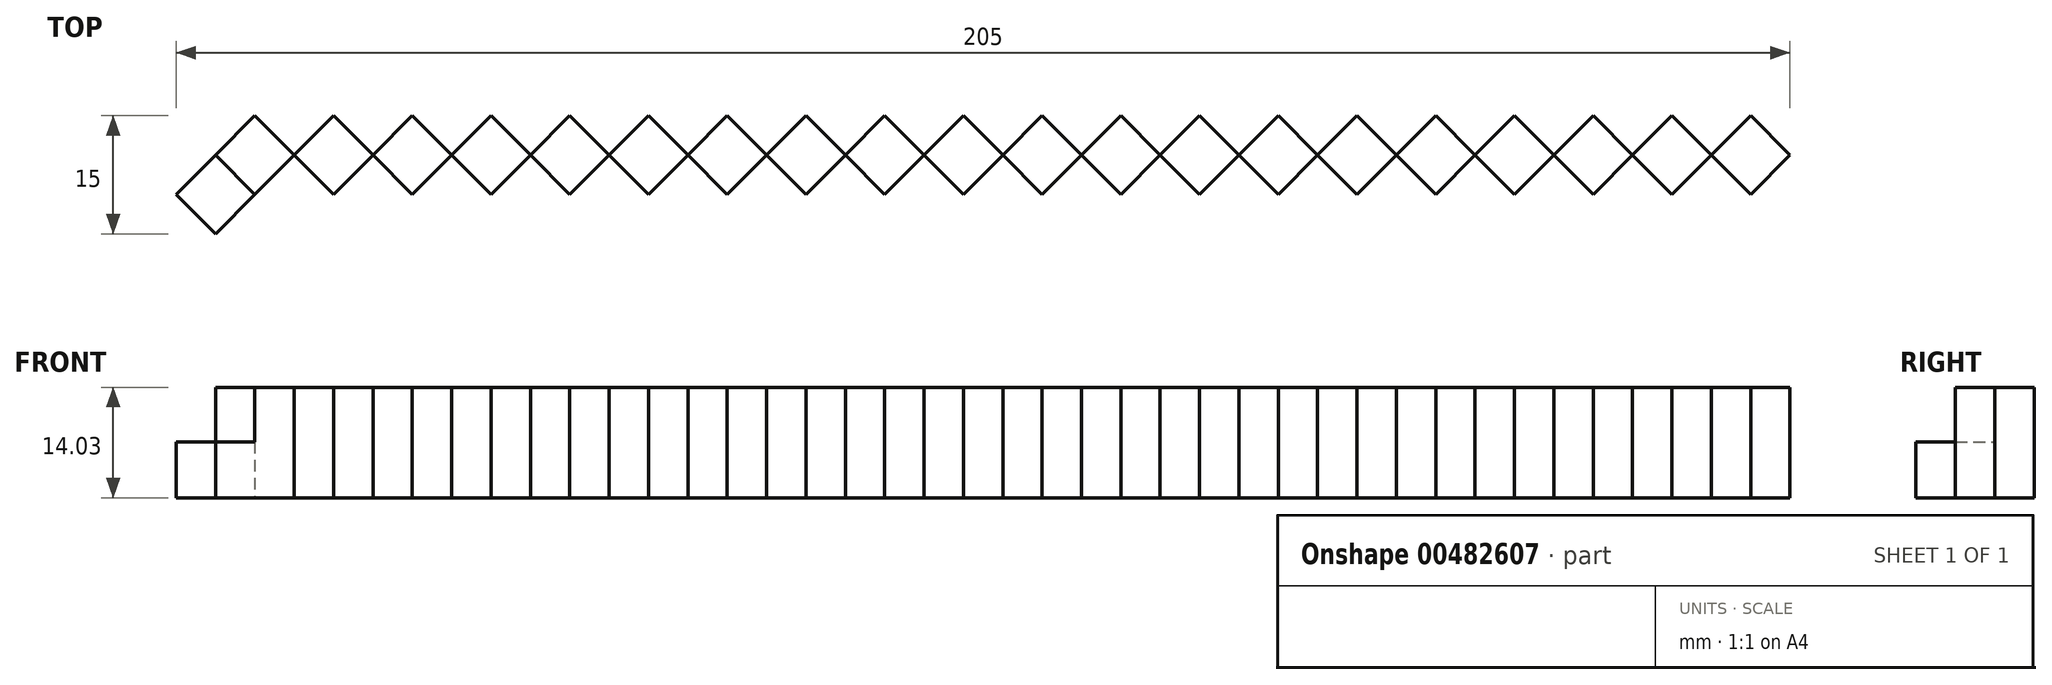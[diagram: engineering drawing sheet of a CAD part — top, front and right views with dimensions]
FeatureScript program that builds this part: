
annotation { "Feature Type Name" : "Feature", "Feature Type Description" : "" }
export const myFeature = defineFeature(function(context is Context, id is Id, definition is map)
    precondition{}
    {
        {
            var Q0;
            Q0=qCreatedBy(makeId("Top.planeOp"),FACE);
            var sketch = newSketch(context, id + "F0", { "sketchPlane" : qUnion([Q0])});
            skLineSegment(sketch, "E0", {"start": v(0, 5) * mm, "end": v(5, 0) * mm});
            skLineSegment(sketch, "E1", {"start": v(5, 0) * mm, "end": v(0, -5) * mm});
            skLineSegment(sketch, "E2", {"start": v(0, -5) * mm, "end": v(-5, 0) * mm});
            skLineSegment(sketch, "E3", {"start": v(-5, 0) * mm, "end": v(0, 5) * mm});
            skLineSegment(sketch, "E4", {"start": v(0, 5) * mm, "end": v(5, 10) * mm});
            skLineSegment(sketch, "E5", {"start": v(5, 10) * mm, "end": v(10, 5) * mm});
            skLineSegment(sketch, "E6", {"start": v(10, 5) * mm, "end": v(5, 0) * mm});
            skLineSegment(sketch, "E7.1.0.0", {"start": v(5, 0) * mm, "end": v(10, 5) * mm});
            skLineSegment(sketch, "E7.1.0.1", {"start": v(15, 0) * mm, "end": v(10, -5) * mm});
            skLineSegment(sketch, "E7.1.0.2", {"start": v(10, -5) * mm, "end": v(5, 0) * mm});
            skLineSegment(sketch, "E7.1.0.3", {"start": v(20, 5) * mm, "end": v(15, 0) * mm});
            skLineSegment(sketch, "E7.1.0.4", {"start": v(10, 5) * mm, "end": v(15, 0) * mm});
            skLineSegment(sketch, "E7.1.0.5", {"start": v(15, 10) * mm, "end": v(20, 5) * mm});
            skLineSegment(sketch, "E7.1.0.6", {"start": v(10, 5) * mm, "end": v(15, 10) * mm});
            skLineSegment(sketch, "E7.2.0.0", {"start": v(15, 0) * mm, "end": v(20, 5) * mm});
            skLineSegment(sketch, "E7.2.0.1", {"start": v(25, 0) * mm, "end": v(20, -5) * mm});
            skLineSegment(sketch, "E7.2.0.2", {"start": v(20, -5) * mm, "end": v(15, 0) * mm});
            skLineSegment(sketch, "E7.2.0.3", {"start": v(30, 5) * mm, "end": v(25, 0) * mm});
            skLineSegment(sketch, "E7.2.0.4", {"start": v(20, 5) * mm, "end": v(25, 0) * mm});
            skLineSegment(sketch, "E7.2.0.5", {"start": v(25, 10) * mm, "end": v(30, 5) * mm});
            skLineSegment(sketch, "E7.2.0.6", {"start": v(20, 5) * mm, "end": v(25, 10) * mm});
            skLineSegment(sketch, "E7.3.0.0", {"start": v(25, 0) * mm, "end": v(30, 5) * mm});
            skLineSegment(sketch, "E7.3.0.1", {"start": v(35, 0) * mm, "end": v(30, -5) * mm});
            skLineSegment(sketch, "E7.3.0.2", {"start": v(30, -5) * mm, "end": v(25, 0) * mm});
            skLineSegment(sketch, "E7.3.0.3", {"start": v(40, 5) * mm, "end": v(35, 0) * mm});
            skLineSegment(sketch, "E7.3.0.4", {"start": v(30, 5) * mm, "end": v(35, 0) * mm});
            skLineSegment(sketch, "E7.3.0.5", {"start": v(35, 10) * mm, "end": v(40, 5) * mm});
            skLineSegment(sketch, "E7.3.0.6", {"start": v(30, 5) * mm, "end": v(35, 10) * mm});
            skLineSegment(sketch, "E7.4.0.0", {"start": v(35, 0) * mm, "end": v(40, 5) * mm});
            skLineSegment(sketch, "E7.4.0.1", {"start": v(45, 0) * mm, "end": v(40, -5) * mm});
            skLineSegment(sketch, "E7.4.0.2", {"start": v(40, -5) * mm, "end": v(35, 0) * mm});
            skLineSegment(sketch, "E7.4.0.3", {"start": v(50, 5) * mm, "end": v(45, 0) * mm});
            skLineSegment(sketch, "E7.4.0.4", {"start": v(40, 5) * mm, "end": v(45, 0) * mm});
            skLineSegment(sketch, "E7.4.0.5", {"start": v(45, 10) * mm, "end": v(50, 5) * mm});
            skLineSegment(sketch, "E7.4.0.6", {"start": v(40, 5) * mm, "end": v(45, 10) * mm});
            skLineSegment(sketch, "E7.5.0.0", {"start": v(45, 0) * mm, "end": v(50, 5) * mm});
            skLineSegment(sketch, "E7.5.0.1", {"start": v(55, 0) * mm, "end": v(50, -5) * mm});
            skLineSegment(sketch, "E7.5.0.2", {"start": v(50, -5) * mm, "end": v(45, 0) * mm});
            skLineSegment(sketch, "E7.5.0.3", {"start": v(60, 5) * mm, "end": v(55, 0) * mm});
            skLineSegment(sketch, "E7.5.0.4", {"start": v(50, 5) * mm, "end": v(55, 0) * mm});
            skLineSegment(sketch, "E7.5.0.5", {"start": v(55, 10) * mm, "end": v(60, 5) * mm});
            skLineSegment(sketch, "E7.5.0.6", {"start": v(50, 5) * mm, "end": v(55, 10) * mm});
            skLineSegment(sketch, "E7.6.0.0", {"start": v(55, 0) * mm, "end": v(60, 5) * mm});
            skLineSegment(sketch, "E7.6.0.1", {"start": v(65, 0) * mm, "end": v(60, -5) * mm});
            skLineSegment(sketch, "E7.6.0.2", {"start": v(60, -5) * mm, "end": v(55, 0) * mm});
            skLineSegment(sketch, "E7.6.0.3", {"start": v(70, 5) * mm, "end": v(65, 0) * mm});
            skLineSegment(sketch, "E7.6.0.4", {"start": v(60, 5) * mm, "end": v(65, 0) * mm});
            skLineSegment(sketch, "E7.6.0.5", {"start": v(65, 10) * mm, "end": v(70, 5) * mm});
            skLineSegment(sketch, "E7.6.0.6", {"start": v(60, 5) * mm, "end": v(65, 10) * mm});
            skLineSegment(sketch, "E7.7.0.0", {"start": v(65, 0) * mm, "end": v(70, 5) * mm});
            skLineSegment(sketch, "E7.7.0.1", {"start": v(75, 0) * mm, "end": v(70, -5) * mm});
            skLineSegment(sketch, "E7.7.0.2", {"start": v(70, -5) * mm, "end": v(65, 0) * mm});
            skLineSegment(sketch, "E7.7.0.3", {"start": v(80, 5) * mm, "end": v(75, 0) * mm});
            skLineSegment(sketch, "E7.7.0.4", {"start": v(70, 5) * mm, "end": v(75, 0) * mm});
            skLineSegment(sketch, "E7.7.0.5", {"start": v(75, 10) * mm, "end": v(80, 5) * mm});
            skLineSegment(sketch, "E7.7.0.6", {"start": v(70, 5) * mm, "end": v(75, 10) * mm});
            skLineSegment(sketch, "E7.8.0.0", {"start": v(75, 0) * mm, "end": v(80, 5) * mm});
            skLineSegment(sketch, "E7.8.0.1", {"start": v(85, 0) * mm, "end": v(80, -5) * mm});
            skLineSegment(sketch, "E7.8.0.2", {"start": v(80, -5) * mm, "end": v(75, 0) * mm});
            skLineSegment(sketch, "E7.8.0.3", {"start": v(90, 5) * mm, "end": v(85, 0) * mm});
            skLineSegment(sketch, "E7.8.0.4", {"start": v(80, 5) * mm, "end": v(85, 0) * mm});
            skLineSegment(sketch, "E7.8.0.5", {"start": v(85, 10) * mm, "end": v(90, 5) * mm});
            skLineSegment(sketch, "E7.8.0.6", {"start": v(80, 5) * mm, "end": v(85, 10) * mm});
            skLineSegment(sketch, "E7.9.0.0", {"start": v(85, 0) * mm, "end": v(90, 5) * mm});
            skLineSegment(sketch, "E7.9.0.1", {"start": v(95, 0) * mm, "end": v(90, -5) * mm});
            skLineSegment(sketch, "E7.9.0.2", {"start": v(90, -5) * mm, "end": v(85, 0) * mm});
            skLineSegment(sketch, "E7.9.0.3", {"start": v(100, 5) * mm, "end": v(95, 0) * mm});
            skLineSegment(sketch, "E7.9.0.4", {"start": v(90, 5) * mm, "end": v(95, 0) * mm});
            skLineSegment(sketch, "E7.9.0.5", {"start": v(95, 10) * mm, "end": v(100, 5) * mm});
            skLineSegment(sketch, "E7.9.0.6", {"start": v(90, 5) * mm, "end": v(95, 10) * mm});
            skLineSegment(sketch, "E7.10.0.0", {"start": v(95, 0) * mm, "end": v(100, 5) * mm});
            skLineSegment(sketch, "E7.10.0.1", {"start": v(105, 0) * mm, "end": v(100, -5) * mm});
            skLineSegment(sketch, "E7.10.0.2", {"start": v(100, -5) * mm, "end": v(95, 0) * mm});
            skLineSegment(sketch, "E7.10.0.3", {"start": v(110, 5) * mm, "end": v(105, 0) * mm});
            skLineSegment(sketch, "E7.10.0.4", {"start": v(100, 5) * mm, "end": v(105, 0) * mm});
            skLineSegment(sketch, "E7.10.0.5", {"start": v(105, 10) * mm, "end": v(110, 5) * mm});
            skLineSegment(sketch, "E7.10.0.6", {"start": v(100, 5) * mm, "end": v(105, 10) * mm});
            skLineSegment(sketch, "E7.11.0.0", {"start": v(105, 0) * mm, "end": v(110, 5) * mm});
            skLineSegment(sketch, "E7.11.0.1", {"start": v(115, 0) * mm, "end": v(110, -5) * mm});
            skLineSegment(sketch, "E7.11.0.2", {"start": v(110, -5) * mm, "end": v(105, 0) * mm});
            skLineSegment(sketch, "E7.11.0.3", {"start": v(120, 5) * mm, "end": v(115, 0) * mm});
            skLineSegment(sketch, "E7.11.0.4", {"start": v(110, 5) * mm, "end": v(115, 0) * mm});
            skLineSegment(sketch, "E7.11.0.5", {"start": v(115, 10) * mm, "end": v(120, 5) * mm});
            skLineSegment(sketch, "E7.11.0.6", {"start": v(110, 5) * mm, "end": v(115, 10) * mm});
            skLineSegment(sketch, "E7.12.0.0", {"start": v(115, 0) * mm, "end": v(120, 5) * mm});
            skLineSegment(sketch, "E7.12.0.1", {"start": v(125, 0) * mm, "end": v(120, -5) * mm});
            skLineSegment(sketch, "E7.12.0.2", {"start": v(120, -5) * mm, "end": v(115, 0) * mm});
            skLineSegment(sketch, "E7.12.0.3", {"start": v(130, 5) * mm, "end": v(125, 0) * mm});
            skLineSegment(sketch, "E7.12.0.4", {"start": v(120, 5) * mm, "end": v(125, 0) * mm});
            skLineSegment(sketch, "E7.12.0.5", {"start": v(125, 10) * mm, "end": v(130, 5) * mm});
            skLineSegment(sketch, "E7.12.0.6", {"start": v(120, 5) * mm, "end": v(125, 10) * mm});
            skLineSegment(sketch, "E7.13.0.0", {"start": v(125, 0) * mm, "end": v(130, 5) * mm});
            skLineSegment(sketch, "E7.13.0.1", {"start": v(135, 0) * mm, "end": v(130, -5) * mm});
            skLineSegment(sketch, "E7.13.0.2", {"start": v(130, -5) * mm, "end": v(125, 0) * mm});
            skLineSegment(sketch, "E7.13.0.3", {"start": v(140, 5) * mm, "end": v(135, 0) * mm});
            skLineSegment(sketch, "E7.13.0.4", {"start": v(130, 5) * mm, "end": v(135, 0) * mm});
            skLineSegment(sketch, "E7.13.0.5", {"start": v(135, 10) * mm, "end": v(140, 5) * mm});
            skLineSegment(sketch, "E7.13.0.6", {"start": v(130, 5) * mm, "end": v(135, 10) * mm});
            skLineSegment(sketch, "E7.14.0.0", {"start": v(135, 0) * mm, "end": v(140, 5) * mm});
            skLineSegment(sketch, "E7.14.0.1", {"start": v(145, 0) * mm, "end": v(140, -5) * mm});
            skLineSegment(sketch, "E7.14.0.2", {"start": v(140, -5) * mm, "end": v(135, 0) * mm});
            skLineSegment(sketch, "E7.14.0.3", {"start": v(150, 5) * mm, "end": v(145, 0) * mm});
            skLineSegment(sketch, "E7.14.0.4", {"start": v(140, 5) * mm, "end": v(145, 0) * mm});
            skLineSegment(sketch, "E7.14.0.5", {"start": v(145, 10) * mm, "end": v(150, 5) * mm});
            skLineSegment(sketch, "E7.14.0.6", {"start": v(140, 5) * mm, "end": v(145, 10) * mm});
            skLineSegment(sketch, "E7.15.0.0", {"start": v(145, 0) * mm, "end": v(150, 5) * mm});
            skLineSegment(sketch, "E7.15.0.1", {"start": v(155, 0) * mm, "end": v(150, -5) * mm});
            skLineSegment(sketch, "E7.15.0.2", {"start": v(150, -5) * mm, "end": v(145, 0) * mm});
            skLineSegment(sketch, "E7.15.0.3", {"start": v(160, 5) * mm, "end": v(155, 0) * mm});
            skLineSegment(sketch, "E7.15.0.4", {"start": v(150, 5) * mm, "end": v(155, 0) * mm});
            skLineSegment(sketch, "E7.15.0.5", {"start": v(155, 10) * mm, "end": v(160, 5) * mm});
            skLineSegment(sketch, "E7.15.0.6", {"start": v(150, 5) * mm, "end": v(155, 10) * mm});
            skLineSegment(sketch, "E7.16.0.0", {"start": v(155, 0) * mm, "end": v(160, 5) * mm});
            skLineSegment(sketch, "E7.16.0.1", {"start": v(165, 0) * mm, "end": v(160, -5) * mm});
            skLineSegment(sketch, "E7.16.0.2", {"start": v(160, -5) * mm, "end": v(155, 0) * mm});
            skLineSegment(sketch, "E7.16.0.3", {"start": v(170, 5) * mm, "end": v(165, 0) * mm});
            skLineSegment(sketch, "E7.16.0.4", {"start": v(160, 5) * mm, "end": v(165, 0) * mm});
            skLineSegment(sketch, "E7.16.0.5", {"start": v(165, 10) * mm, "end": v(170, 5) * mm});
            skLineSegment(sketch, "E7.16.0.6", {"start": v(160, 5) * mm, "end": v(165, 10) * mm});
            skLineSegment(sketch, "E7.17.0.0", {"start": v(165, 0) * mm, "end": v(170, 5) * mm});
            skLineSegment(sketch, "E7.17.0.1", {"start": v(175, 0) * mm, "end": v(170, -5) * mm});
            skLineSegment(sketch, "E7.17.0.2", {"start": v(170, -5) * mm, "end": v(165, 0) * mm});
            skLineSegment(sketch, "E7.17.0.3", {"start": v(180, 5) * mm, "end": v(175, 0) * mm});
            skLineSegment(sketch, "E7.17.0.4", {"start": v(170, 5) * mm, "end": v(175, 0) * mm});
            skLineSegment(sketch, "E7.17.0.5", {"start": v(175, 10) * mm, "end": v(180, 5) * mm});
            skLineSegment(sketch, "E7.17.0.6", {"start": v(170, 5) * mm, "end": v(175, 10) * mm});
            skLineSegment(sketch, "E7.18.0.0", {"start": v(175, 0) * mm, "end": v(180, 5) * mm});
            skLineSegment(sketch, "E7.18.0.1", {"start": v(185, 0) * mm, "end": v(180, -5) * mm});
            skLineSegment(sketch, "E7.18.0.2", {"start": v(180, -5) * mm, "end": v(175, 0) * mm});
            skLineSegment(sketch, "E7.18.0.3", {"start": v(190, 5) * mm, "end": v(185, 0) * mm});
            skLineSegment(sketch, "E7.18.0.4", {"start": v(180, 5) * mm, "end": v(185, 0) * mm});
            skLineSegment(sketch, "E7.18.0.5", {"start": v(185, 10) * mm, "end": v(190, 5) * mm});
            skLineSegment(sketch, "E7.18.0.6", {"start": v(180, 5) * mm, "end": v(185, 10) * mm});
            skLineSegment(sketch, "E7.19.0.0", {"start": v(185, 0) * mm, "end": v(190, 5) * mm});
            skLineSegment(sketch, "E7.19.0.1", {"start": v(195, 0) * mm, "end": v(190, -5) * mm});
            skLineSegment(sketch, "E7.19.0.2", {"start": v(190, -5) * mm, "end": v(185, 0) * mm});
            skLineSegment(sketch, "E7.19.0.3", {"start": v(200, 5) * mm, "end": v(195, 0) * mm});
            skLineSegment(sketch, "E7.19.0.4", {"start": v(190, 5) * mm, "end": v(195, 0) * mm});
            skLineSegment(sketch, "E7.19.0.5", {"start": v(195, 10) * mm, "end": v(200, 5) * mm});
            skLineSegment(sketch, "E7.19.0.6", {"start": v(190, 5) * mm, "end": v(195, 10) * mm});
            skLineSegment(sketch, "E7.direction1", {"start": v(0, -5) * mm, "end": v(10, -5) * mm, "construction": true});
            skSolve(sketch);
        }
        {
            var Q0;
            Q0=makeQuery(id+"F0.imprint","IMPRINT",FACE,{"disambiguationData":[TD([[makeQuery(id+"F0.imprint","IMPRINT",EDGE,{"derivedFrom":sQuery(id+"F0.wireOp",EDGE,"E0")}),-1.0]])]});
            var Q1;
            Q1=makeQuery(id+"F0.imprint","IMPRINT",FACE,{"disambiguationData":[TD([[makeQuery(id+"F0.imprint","IMPRINT",EDGE,{"derivedFrom":sQuery(id+"F0.wireOp",EDGE,"E7.1.0.0")}),-1.0]])]});
            var Q2;
            Q2=makeQuery(id+"F0.imprint","IMPRINT",FACE,{"disambiguationData":[TD([[makeQuery(id+"F0.imprint","IMPRINT",EDGE,{"derivedFrom":sQuery(id+"F0.wireOp",EDGE,"E7.2.0.0")}),-1.0]])]});
            var Q3;
            Q3=makeQuery(id+"F0.imprint","IMPRINT",FACE,{"disambiguationData":[TD([[makeQuery(id+"F0.imprint","IMPRINT",EDGE,{"derivedFrom":sQuery(id+"F0.wireOp",EDGE,"E7.3.0.0")}),-1.0]])]});
            var Q4;
            Q4=makeQuery(id+"F0.imprint","IMPRINT",FACE,{"disambiguationData":[TD([[makeQuery(id+"F0.imprint","IMPRINT",EDGE,{"derivedFrom":sQuery(id+"F0.wireOp",EDGE,"E7.4.0.0")}),-1.0]])]});
            var Q5;
            Q5=makeQuery(id+"F0.imprint","IMPRINT",FACE,{"disambiguationData":[TD([[makeQuery(id+"F0.imprint","IMPRINT",EDGE,{"derivedFrom":sQuery(id+"F0.wireOp",EDGE,"E7.5.0.0")}),-1.0]])]});
            var Q6;
            Q6=makeQuery(id+"F0.imprint","IMPRINT",FACE,{"disambiguationData":[TD([[makeQuery(id+"F0.imprint","IMPRINT",EDGE,{"derivedFrom":sQuery(id+"F0.wireOp",EDGE,"E7.6.0.0")}),-1.0]])]});
            var Q7;
            Q7=makeQuery(id+"F0.imprint","IMPRINT",FACE,{"disambiguationData":[TD([[makeQuery(id+"F0.imprint","IMPRINT",EDGE,{"derivedFrom":sQuery(id+"F0.wireOp",EDGE,"E7.7.0.0")}),-1.0]])]});
            var Q8;
            Q8=makeQuery(id+"F0.imprint","IMPRINT",FACE,{"disambiguationData":[TD([[makeQuery(id+"F0.imprint","IMPRINT",EDGE,{"derivedFrom":sQuery(id+"F0.wireOp",EDGE,"E7.8.0.0")}),-1.0]])]});
            var Q9;
            Q9=makeQuery(id+"F0.imprint","IMPRINT",FACE,{"disambiguationData":[TD([[makeQuery(id+"F0.imprint","IMPRINT",EDGE,{"derivedFrom":sQuery(id+"F0.wireOp",EDGE,"E7.9.0.0")}),-1.0]])]});
            var Q10;
            Q10=makeQuery(id+"F0.imprint","IMPRINT",FACE,{"disambiguationData":[TD([[makeQuery(id+"F0.imprint","IMPRINT",EDGE,{"derivedFrom":sQuery(id+"F0.wireOp",EDGE,"E7.10.0.0")}),-1.0]])]});
            var Q11;
            Q11=makeQuery(id+"F0.imprint","IMPRINT",FACE,{"disambiguationData":[TD([[makeQuery(id+"F0.imprint","IMPRINT",EDGE,{"derivedFrom":sQuery(id+"F0.wireOp",EDGE,"E7.11.0.0")}),-1.0]])]});
            var Q12;
            Q12=makeQuery(id+"F0.imprint","IMPRINT",FACE,{"disambiguationData":[TD([[makeQuery(id+"F0.imprint","IMPRINT",EDGE,{"derivedFrom":sQuery(id+"F0.wireOp",EDGE,"E7.12.0.0")}),-1.0]])]});
            var Q13;
            Q13=makeQuery(id+"F0.imprint","IMPRINT",FACE,{"disambiguationData":[TD([[makeQuery(id+"F0.imprint","IMPRINT",EDGE,{"derivedFrom":sQuery(id+"F0.wireOp",EDGE,"E7.13.0.0")}),-1.0]])]});
            var Q14;
            Q14=makeQuery(id+"F0.imprint","IMPRINT",FACE,{"disambiguationData":[TD([[makeQuery(id+"F0.imprint","IMPRINT",EDGE,{"derivedFrom":sQuery(id+"F0.wireOp",EDGE,"E7.14.0.0")}),-1.0]])]});
            var Q15;
            Q15=makeQuery(id+"F0.imprint","IMPRINT",FACE,{"disambiguationData":[TD([[makeQuery(id+"F0.imprint","IMPRINT",EDGE,{"derivedFrom":sQuery(id+"F0.wireOp",EDGE,"E7.15.0.0")}),-1.0]])]});
            var Q16;
            Q16=makeQuery(id+"F0.imprint","IMPRINT",FACE,{"disambiguationData":[TD([[makeQuery(id+"F0.imprint","IMPRINT",EDGE,{"derivedFrom":sQuery(id+"F0.wireOp",EDGE,"E7.16.0.0")}),-1.0]])]});
            var Q17;
            Q17=makeQuery(id+"F0.imprint","IMPRINT",FACE,{"disambiguationData":[TD([[makeQuery(id+"F0.imprint","IMPRINT",EDGE,{"derivedFrom":sQuery(id+"F0.wireOp",EDGE,"E7.17.0.0")}),-1.0]])]});
            var Q18;
            Q18=makeQuery(id+"F0.imprint","IMPRINT",FACE,{"disambiguationData":[TD([[makeQuery(id+"F0.imprint","IMPRINT",EDGE,{"derivedFrom":sQuery(id+"F0.wireOp",EDGE,"E7.18.0.0")}),-1.0]])]});
            var Q19;
            Q19=makeQuery(id+"F0.imprint","IMPRINT",FACE,{"disambiguationData":[TD([[makeQuery(id+"F0.imprint","IMPRINT",EDGE,{"derivedFrom":sQuery(id+"F0.wireOp",EDGE,"E7.19.0.0")}),-1.0]])]});
            extrude(context, id + "F1", {"entities" : qUnion([Q0, Q1, Q2, Q3, Q4, Q5, Q6, Q7, Q8, Q9, Q10, Q11, Q12, Q13, Q14, Q15, Q16, Q17, Q18, Q19]), "depth" : 7.07 * mm, "offsetDistance" : 25 * mm});
        }
        {
            var Q0;
            Q0=makeQuery(id+"F0.imprint","IMPRINT",FACE,{"disambiguationData":[TD([[makeQuery(id+"F0.imprint","IMPRINT",EDGE,{"derivedFrom":sQuery(id+"F0.wireOp",EDGE,"E7.1.0.4")}),1.0]])]});
            var Q1;
            Q1=makeQuery(id+"F0.imprint","IMPRINT",FACE,{"disambiguationData":[TD([[makeQuery(id+"F0.imprint","IMPRINT",EDGE,{"derivedFrom":sQuery(id+"F0.wireOp",EDGE,"E7.2.0.4")}),1.0]])]});
            var Q2;
            Q2=makeQuery(id+"F0.imprint","IMPRINT",FACE,{"disambiguationData":[TD([[makeQuery(id+"F0.imprint","IMPRINT",EDGE,{"derivedFrom":sQuery(id+"F0.wireOp",EDGE,"E7.3.0.4")}),1.0]])]});
            var Q3;
            Q3=makeQuery(id+"F0.imprint","IMPRINT",FACE,{"disambiguationData":[TD([[makeQuery(id+"F0.imprint","IMPRINT",EDGE,{"derivedFrom":sQuery(id+"F0.wireOp",EDGE,"E0")}),1.0]])]});
            var Q4;
            Q4=makeQuery(id+"F0.imprint","IMPRINT",FACE,{"disambiguationData":[TD([[makeQuery(id+"F0.imprint","IMPRINT",EDGE,{"derivedFrom":sQuery(id+"F0.wireOp",EDGE,"E7.4.0.4")}),1.0]])]});
            var Q5;
            Q5=makeQuery(id+"F0.imprint","IMPRINT",FACE,{"disambiguationData":[TD([[makeQuery(id+"F0.imprint","IMPRINT",EDGE,{"derivedFrom":sQuery(id+"F0.wireOp",EDGE,"E7.9.0.4")}),1.0]])]});
            var Q6;
            Q6=makeQuery(id+"F0.imprint","IMPRINT",FACE,{"disambiguationData":[TD([[makeQuery(id+"F0.imprint","IMPRINT",EDGE,{"derivedFrom":sQuery(id+"F0.wireOp",EDGE,"E7.10.0.4")}),1.0]])]});
            var Q7;
            Q7=makeQuery(id+"F0.imprint","IMPRINT",FACE,{"disambiguationData":[TD([[makeQuery(id+"F0.imprint","IMPRINT",EDGE,{"derivedFrom":sQuery(id+"F0.wireOp",EDGE,"E7.11.0.4")}),1.0]])]});
            var Q8;
            Q8=makeQuery(id+"F0.imprint","IMPRINT",FACE,{"disambiguationData":[TD([[makeQuery(id+"F0.imprint","IMPRINT",EDGE,{"derivedFrom":sQuery(id+"F0.wireOp",EDGE,"E7.12.0.4")}),1.0]])]});
            var Q9;
            Q9=makeQuery(id+"F0.imprint","IMPRINT",FACE,{"disambiguationData":[TD([[makeQuery(id+"F0.imprint","IMPRINT",EDGE,{"derivedFrom":sQuery(id+"F0.wireOp",EDGE,"E7.13.0.4")}),1.0]])]});
            var Q10;
            Q10=makeQuery(id+"F0.imprint","IMPRINT",FACE,{"disambiguationData":[TD([[makeQuery(id+"F0.imprint","IMPRINT",EDGE,{"derivedFrom":sQuery(id+"F0.wireOp",EDGE,"E7.14.0.4")}),1.0]])]});
            var Q11;
            Q11=makeQuery(id+"F0.imprint","IMPRINT",FACE,{"disambiguationData":[TD([[makeQuery(id+"F0.imprint","IMPRINT",EDGE,{"derivedFrom":sQuery(id+"F0.wireOp",EDGE,"E7.15.0.4")}),1.0]])]});
            var Q12;
            Q12=makeQuery(id+"F0.imprint","IMPRINT",FACE,{"disambiguationData":[TD([[makeQuery(id+"F0.imprint","IMPRINT",EDGE,{"derivedFrom":sQuery(id+"F0.wireOp",EDGE,"E7.16.0.4")}),1.0]])]});
            var Q13;
            Q13=makeQuery(id+"F0.imprint","IMPRINT",FACE,{"disambiguationData":[TD([[makeQuery(id+"F0.imprint","IMPRINT",EDGE,{"derivedFrom":sQuery(id+"F0.wireOp",EDGE,"E7.17.0.4")}),1.0]])]});
            var Q14;
            Q14=makeQuery(id+"F0.imprint","IMPRINT",FACE,{"disambiguationData":[TD([[makeQuery(id+"F0.imprint","IMPRINT",EDGE,{"derivedFrom":sQuery(id+"F0.wireOp",EDGE,"E7.18.0.4")}),1.0]])]});
            var Q15;
            Q15=makeQuery(id+"F0.imprint","IMPRINT",FACE,{"disambiguationData":[TD([[makeQuery(id+"F0.imprint","IMPRINT",EDGE,{"derivedFrom":sQuery(id+"F0.wireOp",EDGE,"E7.19.0.3")}),-1.0]])]});
            var Q16;
            Q16=makeQuery(id+"F0.imprint","IMPRINT",FACE,{"disambiguationData":[TD([[makeQuery(id+"F0.imprint","IMPRINT",EDGE,{"derivedFrom":sQuery(id+"F0.wireOp",EDGE,"E7.8.0.4")}),1.0]])]});
            var Q17;
            Q17=makeQuery(id+"F0.imprint","IMPRINT",FACE,{"disambiguationData":[TD([[makeQuery(id+"F0.imprint","IMPRINT",EDGE,{"derivedFrom":sQuery(id+"F0.wireOp",EDGE,"E7.7.0.4")}),1.0]])]});
            var Q18;
            Q18=makeQuery(id+"F0.imprint","IMPRINT",FACE,{"disambiguationData":[TD([[makeQuery(id+"F0.imprint","IMPRINT",EDGE,{"derivedFrom":sQuery(id+"F0.wireOp",EDGE,"E7.5.0.4")}),1.0]])]});
            var Q19;
            Q19=makeQuery(id+"F0.imprint","IMPRINT",FACE,{"disambiguationData":[TD([[makeQuery(id+"F0.imprint","IMPRINT",EDGE,{"derivedFrom":sQuery(id+"F0.wireOp",EDGE,"E7.6.0.4")}),1.0]])]});
            extrude(context, id + "F2", {"entities" : qUnion([Q0, Q1, Q2, Q3, Q4, Q5, Q6, Q7, Q8, Q9, Q10, Q11, Q12, Q13, Q14, Q15, Q16, Q17, Q18, Q19]), "operationType" : NewBodyOperationType.ADD, "depth" : 2 * 7.02 * mm, "offsetDistance" : 25 * mm});
        }
    });
